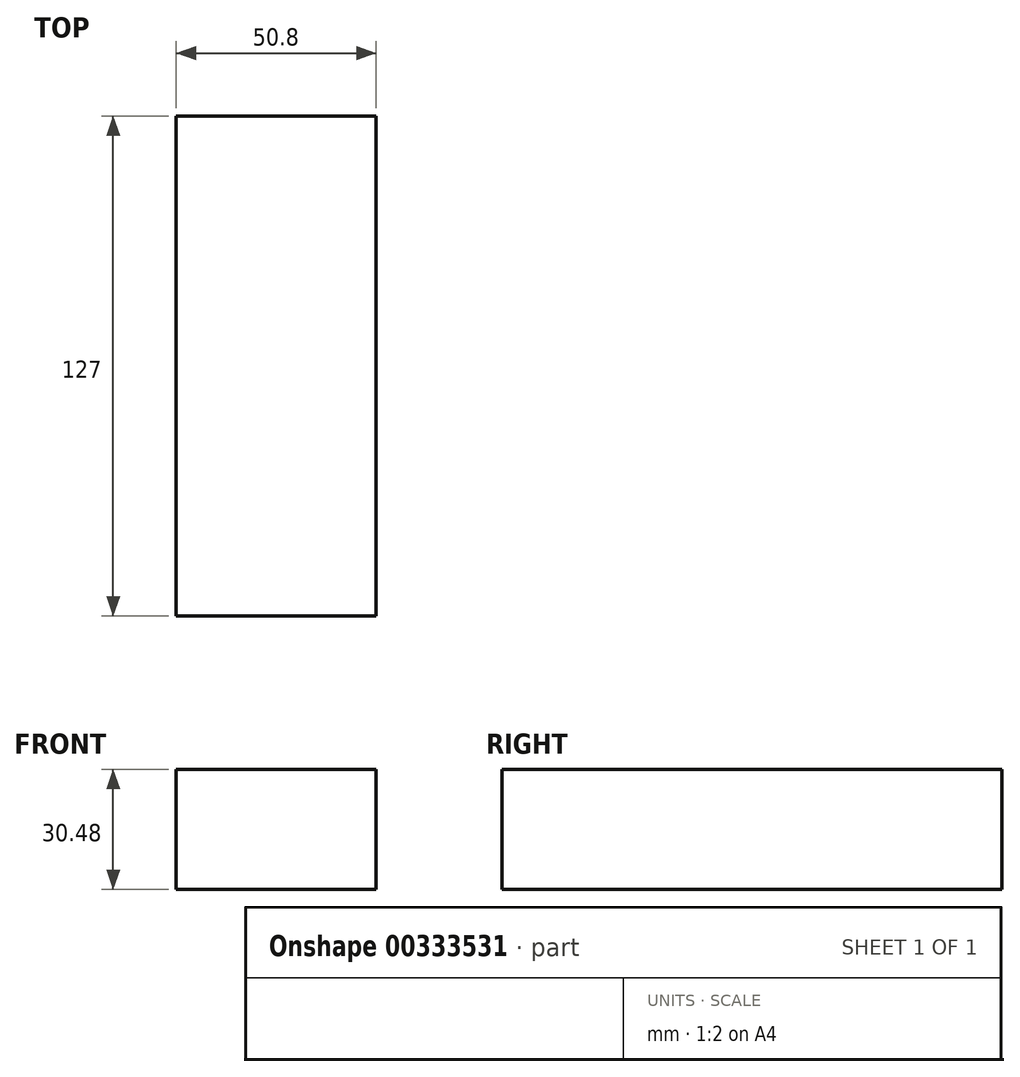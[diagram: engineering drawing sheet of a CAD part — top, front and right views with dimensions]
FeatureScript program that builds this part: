
annotation { "Feature Type Name" : "Feature", "Feature Type Description" : "" }
export const myFeature = defineFeature(function(context is Context, id is Id, definition is map)
    precondition{}
    {
        {
            var Q0;
            Q0=qCreatedBy(makeId("Right.planeOp"),FACE);
            var sketch = newSketch(context, id + "F0", { "sketchPlane" : qUnion([Q0])});
            skLineSegment(sketch, "E0.bottom", {"start": v(-63.5, 15.24) * mm, "end": v(63.5, 15.24) * mm});
            skLineSegment(sketch, "E0.top", {"start": v(-63.5, -15.24) * mm, "end": v(63.5, -15.24) * mm});
            skLineSegment(sketch, "E0.left", {"start": v(-63.5, 15.24) * mm, "end": v(-63.5, -15.24) * mm});
            skLineSegment(sketch, "E0.right", {"start": v(63.5, 15.24) * mm, "end": v(63.5, -15.24) * mm});
            skPoint(sketch, "E0.middle", {"position": v(0, 0) * mm});
            skSolve(sketch);
        }
        {
            var Q0;
            Q0 = qSketchRegion(id + "F0", true);
            extrude(context, id + "F1", {"entities" : qUnion([Q0]), "depth" : 50.8 * mm, "offsetDistance" : 25.4 * mm, "symmetric" : true});
        }
    });
